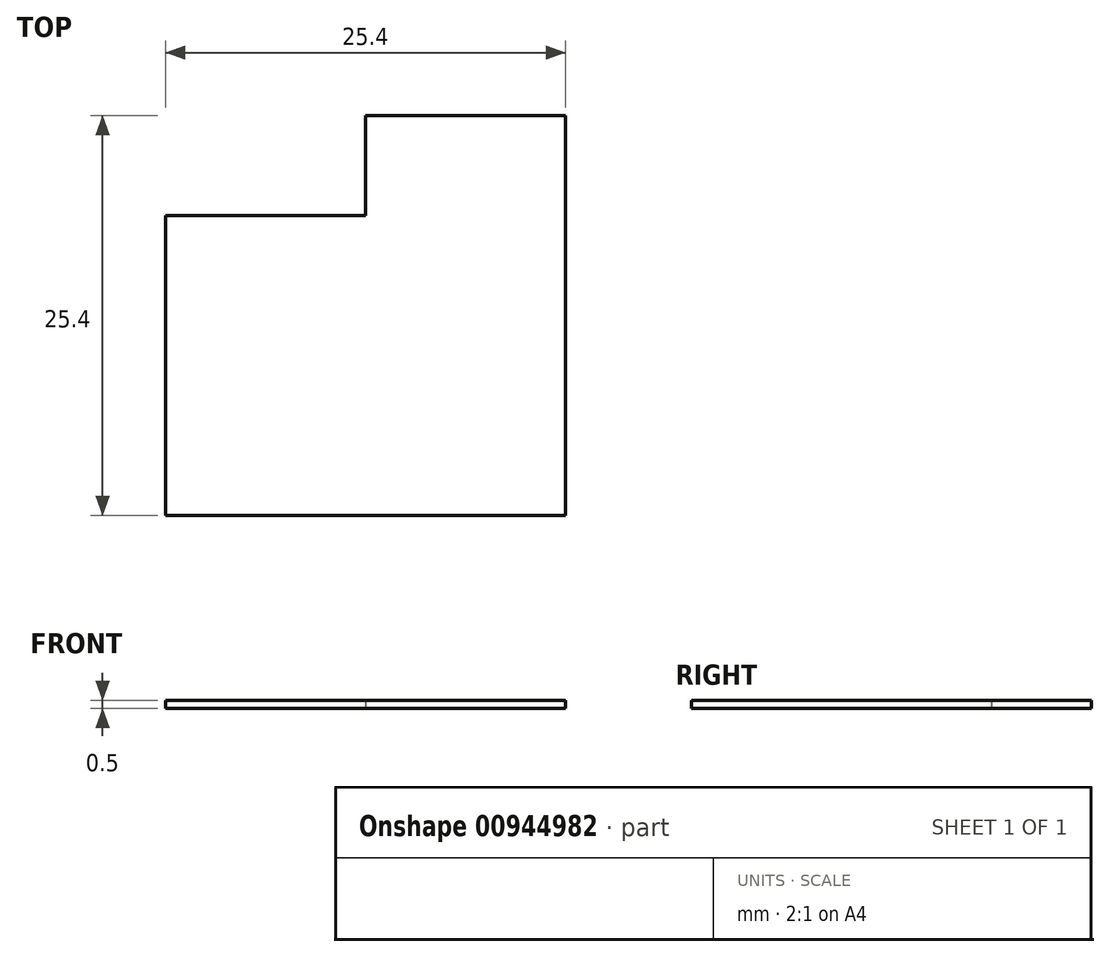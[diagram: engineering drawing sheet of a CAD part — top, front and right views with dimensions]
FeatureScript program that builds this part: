
annotation { "Feature Type Name" : "Feature", "Feature Type Description" : "" }
export const myFeature = defineFeature(function(context is Context, id is Id, definition is map)
    precondition{}
    {
        {
            var Q0;
            Q0=qCreatedBy(makeId("Top.planeOp"),FACE);
            var sketch = newSketch(context, id + "F0", { "sketchPlane" : qUnion([Q0])});
            skLineSegment(sketch, "E0.bottom", {"start": v(0, 12.7) * mm, "end": v(12.7, 12.7) * mm});
            skLineSegment(sketch, "E0.top", {"start": v(-12.7, -12.7) * mm, "end": v(12.7, -12.7) * mm});
            skLineSegment(sketch, "E0.left", {"start": v(-12.7, 6.35) * mm, "end": v(-12.7, -12.7) * mm});
            skLineSegment(sketch, "E0.right", {"start": v(12.7, 12.7) * mm, "end": v(12.7, -12.7) * mm});
            skLineSegment(sketch, "E1.top", {"start": v(-12.7, 6.35) * mm, "end": v(0, 6.35) * mm});
            skLineSegment(sketch, "E1.right", {"start": v(0, 12.7) * mm, "end": v(0, 6.35) * mm});
            skSolve(sketch);
        }
        {
            var Q0;
            Q0 = qSketchRegion(id + "F0", true);
            extrude(context, id + "F1", {"entities" : qUnion([Q0]), "depth" : .5 * mm, "offsetDistance" : 25.4 * mm});
        }
    });
